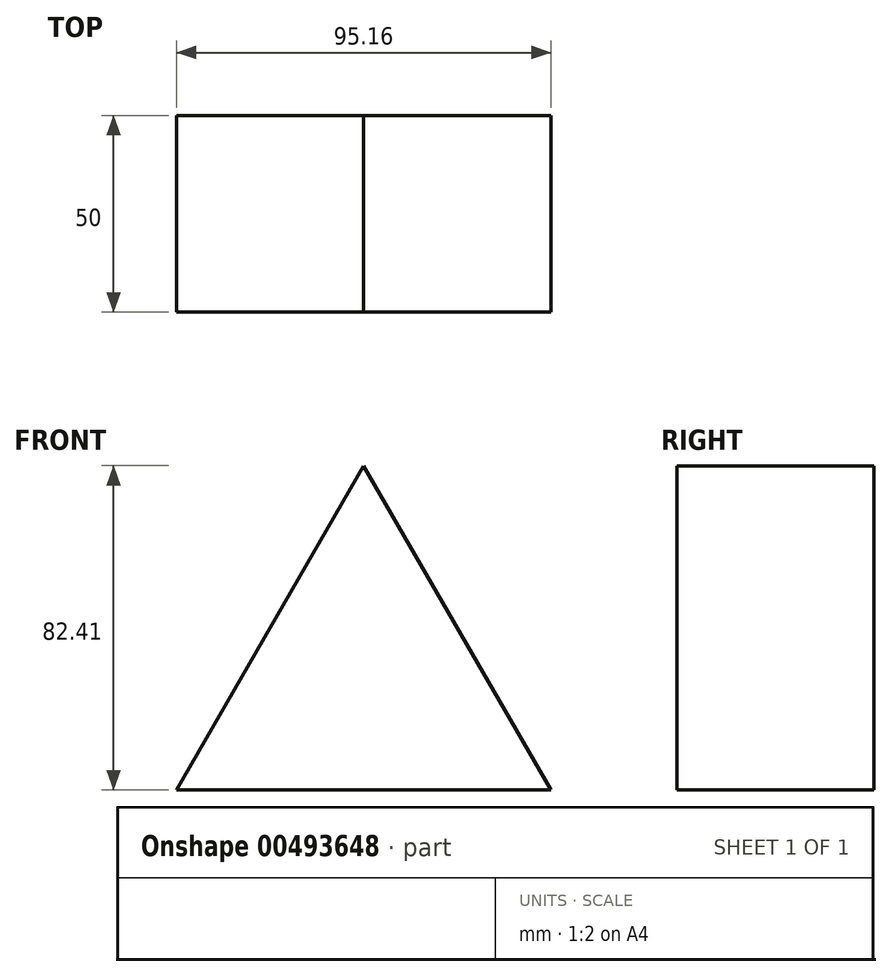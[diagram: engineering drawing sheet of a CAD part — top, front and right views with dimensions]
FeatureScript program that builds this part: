
annotation { "Feature Type Name" : "Feature", "Feature Type Description" : "" }
export const myFeature = defineFeature(function(context is Context, id is Id, definition is map)
    precondition{}
    {
        {
            var Q0;
            Q0=qCreatedBy(makeId("Front.planeOp"),FACE);
            var sketch = newSketch(context, id + "F0", { "sketchPlane" : qUnion([Q0])});
            skCircle(sketch, "E0.cCircle", {"center": v(0, 0) * mm, "radius": 54.94 * mm, "construction": true});
            skLineSegment(sketch, "E0.0", {"start": v(47.58, -27.47) * mm, "end": v(-47.58, -27.47) * mm});
            skLineSegment(sketch, "E0.1", {"start": v(-47.58, -27.47) * mm, "end": v(0, 54.94) * mm});
            skLineSegment(sketch, "E0.2", {"start": v(0, 54.94) * mm, "end": v(47.58, -27.47) * mm});
            skSolve(sketch);
        }
        {
            var Q0;
            Q0=makeQuery(id+"F0.imprint","IMPRINT",FACE,{"disambiguationData":[TD([[makeQuery(id+"F0.imprint","IMPRINT",EDGE,{"derivedFrom":sQuery(id+"F0.wireOp",EDGE,"E0.0")}),-1.0]])]});
            extrude(context, id + "F1", {"entities" : qUnion([Q0]), "endBound" : BoundingType.SYMMETRIC, "depth" : 50 * mm});
        }
    });
